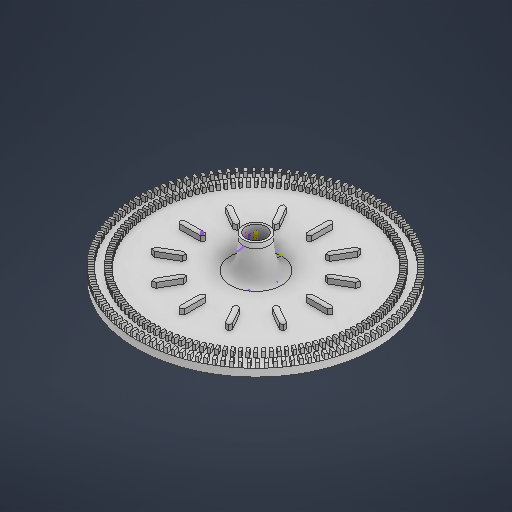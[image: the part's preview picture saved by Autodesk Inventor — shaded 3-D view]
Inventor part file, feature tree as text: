
AUTODESK INVENTOR PART (.ipt)
format: ipt  version: 2025 (Build 290162000, 162)  size: 4,347,904 bytes
history: native  units: mm
features: sketch x8, other x4, extrude x3, pattern_circular x2, revolve x1, projected_geometry x1
ambient origin geometry x8: Origin, YZ Plane, XZ Plane, XY Plane, X Axis, Y Axis, Z Axis, Center Point
bodies: Body1 (feature_tree)
feature tree (19):
  other  "Твердое тело1"
  revolve  "Вращение1"
  extrude  "Выдавливание1"  Depth=1.5mm
  pattern_circular  "Круговой массив1"  Angle=360.0deg  [1 undecoded]
  other  "РабПлоскость5"
  sketch  "Эскиз8"
  other  "РабПлоскость6"
  sketch  "Эскиз9"
  sketch  "Эскиз12"
  sketch  "Эскиз13"
  extrude  "Выдавливание2"  Depth=1.0mm
  extrude  "Выдавливание3"  Depth=0.5mm
  pattern_circular  "Круговой массив3"  [2 undecoded]
  sketch  "Эскиз1"
  sketch  "Эскиз2"
  projected_geometry  "Спроецированная петля2"
  other  "Твердое тело2"
  sketch  "Эскиз14"
  sketch  "Эскиз15"
note: 3 required parameter values undecoded (feature->parameter linkage not recoverable at this tier; creation-order binding heuristic only, values carry confidence <= 0.55)
